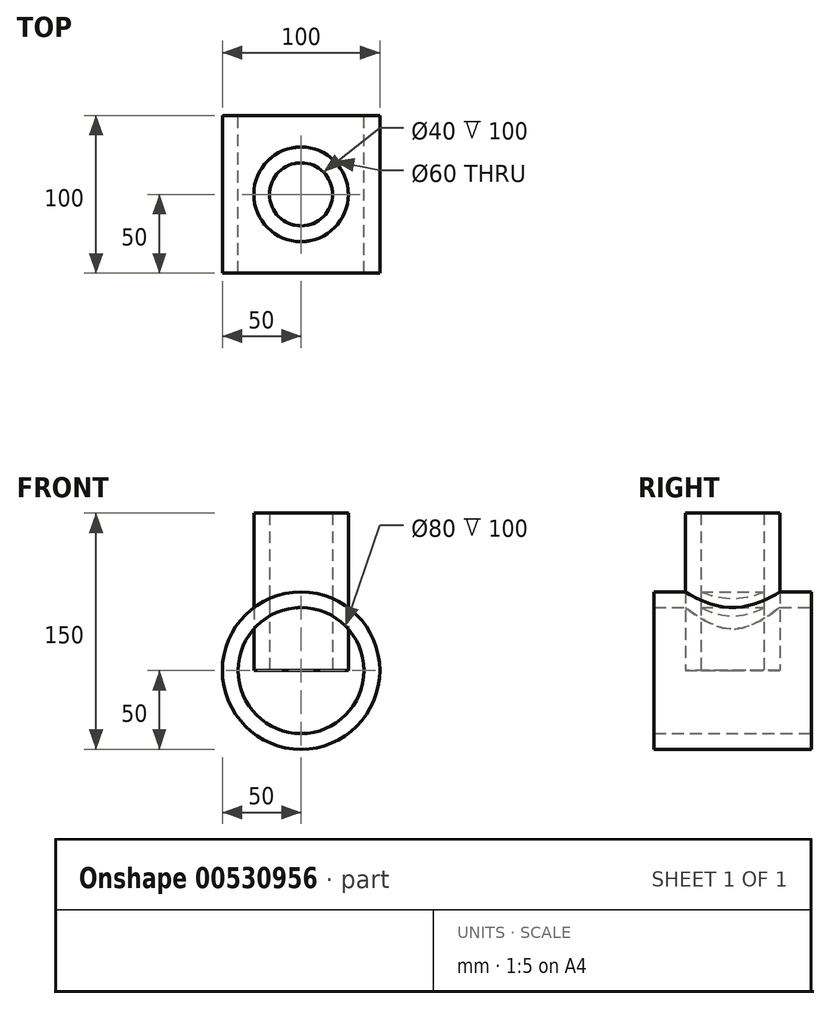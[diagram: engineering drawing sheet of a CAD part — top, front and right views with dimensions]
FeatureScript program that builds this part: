
annotation { "Feature Type Name" : "Feature", "Feature Type Description" : "" }
export const myFeature = defineFeature(function(context is Context, id is Id, definition is map)
    precondition{}
    {
        {
            var Q0;
            Q0=qCreatedBy(makeId("Front.planeOp"),FACE);
            var sketch = newSketch(context, id + "F0", { "sketchPlane" : qUnion([Q0])});
            skCircle(sketch, "E0", {"center": v(0, 0) * mm, "radius": 50 * mm});
            skCircle(sketch, "E1", {"center": v(0, 0) * mm, "radius": 40 * mm});
            skSolve(sketch);
        }
        {
            var Q0;
            Q0=makeQuery(id+"F0.imprint","IMPRINT",FACE,{"disambiguationData":[TD([[makeQuery(id+"F0.imprint","IMPRINT",EDGE,{"derivedFrom":sQuery(id+"F0.wireOp",EDGE,"E0")}),1.0]])]});
            extrude(context, id + "F1", {"entities" : qUnion([Q0]), "endBound" : BoundingType.SYMMETRIC, "depth" : 100 * mm, "offsetDistance" : 25 * mm});
        }
        {
            var Q0;
            Q0=qCreatedBy(makeId("Top.planeOp"),FACE);
            var sketch = newSketch(context, id + "F2", { "sketchPlane" : qUnion([Q0])});
            skCircle(sketch, "E2", {"center": v(0, 0) * mm, "radius": 30 * mm});
            skCircle(sketch, "E3", {"center": v(0, 0) * mm, "radius": 20 * mm});
            skSolve(sketch);
        }
        {
            var Q0;
            Q0=makeQuery(id+"F2.imprint","IMPRINT",FACE,{"disambiguationData":[TD([[makeQuery(id+"F2.imprint","IMPRINT",EDGE,{"derivedFrom":sQuery(id+"F2.wireOp",EDGE,"E2")}),1.0]])]});
            extrude(context, id + "F3", {"entities" : qUnion([Q0]), "depth" : 100 * mm, "offsetDistance" : 25 * mm});
        }
        {
            var Q0;
            Q0=makeQuery(id+"F3.opExtrude","SWEPT_BODY",BODY,{"disambiguationData":[OSD([sQuery(id+"F2.wireOp",EDGE,"E2"),sQuery(id+"F2.wireOp",EDGE,"E3")])]});
            var Q1;
            Q1=makeQuery(id+"F1.opExtrude","SWEPT_BODY",BODY,{"disambiguationData":[OSD([sQuery(id+"F0.wireOp",EDGE,"E0"),sQuery(id+"F0.wireOp",EDGE,"E1")])]});
            booleanBodies(context, id + "F4", {"operationType" : BooleanOperationType.SUBTRACTION, "tools" : qUnion([Q0]), "targets" : qUnion([Q1]), "keepTools" : true});
        }
    });
